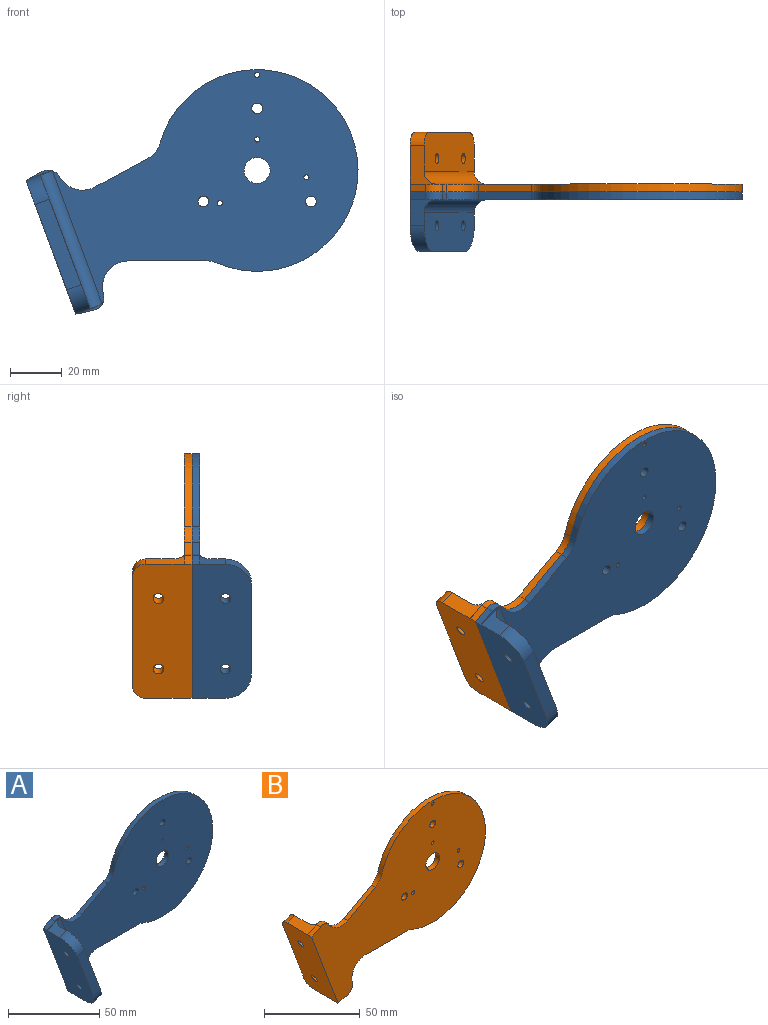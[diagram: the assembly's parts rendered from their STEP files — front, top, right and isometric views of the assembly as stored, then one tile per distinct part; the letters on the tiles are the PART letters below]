
ASSEMBLY  parts=2 mates=1
PART A: 37 faces, bbox 128.4x23x94.6 mm
  f0: plane 118.22x90.64mm, normal (0,-1,0), area 6030.9mm2, adj f6,f7,f8,f9,f10,f11,f12,f18
  f1: plane 10.12x3.79mm, normal (0,-1,0), area 6.4mm2, adj f3,f14,f27
  f2: plane 6.17x3.31mm, normal (-0.47,0,0.88), area 21mm2, adj f4,f5,f13,f26
  f3: plane 6.96x3mm, normal (0.22,0,-0.98), area 21.4mm2, adj f1,f5,f13,f27
  f4: plane 9.91x3.91mm, normal (0,-1,0), area 5.9mm2, adj f2,f15,f26
  f5: plane 128.4x94.58mm, normal (0,1,0), area 6644.3mm2, adj f2,f3,f6,f7,f8,f9,f10,f11
  f6: cylinder r=1mm len=3mm, axis (0,-1,0), area 18.8mm2, adj f0,f5
  f7: cylinder r=1mm len=3mm, axis (0,-1,0), area 18.8mm2, adj f0,f5
  f8: cylinder r=39mm len=78mm, axis (0,-1,0), area 566.8mm2, adj f0,f5,f25,f31
  f9: cylinder r=2.1mm len=4.2mm, axis (0,1,0), area 39.6mm2, adj f0,f5
  f10: cylinder r=2.1mm len=4.2mm, axis (0,1,0), area 39.6mm2, adj f0,f5
  f11: cylinder r=2.1mm len=4.2mm, axis (0,1,0), area 39.6mm2, adj f0,f5
  f12: cylinder r=5mm len=10mm, axis (0,1,0), area 94.2mm2, adj f0,f5
  f13: plane 51.83x23.01mm, normal (-0.94,0,-0.35), area 1202.4mm2, adj f2,f3,f5,f14,f15,f16,f20,f21
  f14: plane 10.12x10mm, normal (0.35,0,-0.94), area 64.8mm2, adj f1,f13,f17,f32,f35
  f15: plane 10x9.91mm, normal (-0.35,0,0.94), area 63.4mm2, adj f4,f13,f17,f34,f36
  f16: plane 35.12x17.85mm, normal (0,-1,0), area 207.3mm2, adj f13,f17,f35,f36
  f17: plane 51.77x19.41mm, normal (0.94,0,0.35), area 760mm2, adj f14,f15,f16,f20,f21,f32,f33,f34
  f18: cylinder r=1mm len=3mm, axis (0,-1,0), area 18.8mm2, adj f0,f5
  f19: cylinder r=1mm len=3mm, axis (0,-1,0), area 18.8mm2, adj f0,f5
  f20: cylinder r=2.05mm len=6.98mm, axis (0.94,0,0.35), area 76.1mm2, adj f13,f17
  f21: cylinder r=2.05mm len=6.91mm, axis (0.94,0,0.35), area 75.2mm2, adj f13,f17
  f22: plane 3x1.97mm, normal (0.79,0,0.61), area 7.5mm2, adj f0,f5,f23,f26
  f23: cylinder r=10mm len=12.64mm, axis (0,1,0), area 42.1mm2, adj f0,f5,f22,f24
  f24: plane 20.36x10.99mm, normal (-0.48,0,0.88), area 69.4mm2, adj f0,f5,f23,f25
  f25: cylinder r=10mm len=6.07mm, axis (0,1,0), area 24mm2, adj f0,f5,f8,f24
  f26: cylinder r=5mm len=6.31mm, axis (0,1,0), area 21mm2, adj f0,f2,f4,f5,f22,f34
  f27: cylinder r=5mm len=5.97mm, axis (0,1,0), area 23.6mm2, adj f0,f1,f3,f5,f28,f32
  f28: plane 3x0.92mm, normal (0.98,0,0.22), area 2.8mm2, adj f0,f5,f27,f29
  f29: cylinder r=10mm len=12.18mm, axis (0,1,0), area 53.7mm2, adj f0,f5,f28,f30
  f30: plane 30.35x3mm, normal (0,0,-1), area 91.1mm2, adj f0,f5,f29,f31
  f31: cylinder r=10mm len=3.97mm, axis (0,1,0), area 12.3mm2, adj f0,f5,f8,f30
  f32: bspline ~5.37x5.15mm, area 0.9mm2, adj f14,f17,f27,f33
  f33: cylinder r=5mm len=53.26mm, axis (-0.35,0,0.94), area 432mm2, adj f0,f17,f32,f34
  f34: bspline ~5.29x5.25mm, area 1.3mm2, adj f15,f17,f26,f33
  f35: cylinder r=10mm len=11.45mm, axis (-0.94,0,-0.35), area 93.1mm2, adj f13,f14,f16,f17
  f36: cylinder r=10mm len=11.41mm, axis (0.94,0,0.35), area 91.4mm2, adj f13,f15,f16,f17
PART B: 37 faces, bbox 128.4x23x94.6 mm
  f0: plane 10.12x3.79mm, normal (0,1,0), area 6.4mm2, adj f6,f14,f30
  f1: plane 118.22x90.64mm, normal (0,1,0), area 6030.9mm2, adj f4,f5,f7,f8,f9,f10,f11,f18
  f2: plane 6.17x3.31mm, normal (-0.47,0,0.88), area 21mm2, adj f3,f12,f13,f31
  f3: plane 128.4x94.58mm, normal (0,-1,0), area 6644.3mm2, adj f2,f4,f5,f6,f7,f8,f9,f10
  f4: cylinder r=1mm len=3mm, axis (0,1,0), area 18.8mm2, adj f1,f3
  f5: cylinder r=1mm len=3mm, axis (0,1,0), area 18.8mm2, adj f1,f3
  f6: plane 6.96x3mm, normal (0.22,0,-0.98), area 21.4mm2, adj f0,f3,f13,f30
  f7: cylinder r=39mm len=78mm, axis (0,1,0), area 566.8mm2, adj f1,f3,f27,f28
  f8: cylinder r=2.1mm len=4.2mm, axis (0,-1,0), area 39.6mm2, adj f1,f3
  f9: cylinder r=2.1mm len=4.2mm, axis (0,-1,0), area 39.6mm2, adj f1,f3
  f10: cylinder r=2.1mm len=4.2mm, axis (0,-1,0), area 39.6mm2, adj f1,f3
  f11: cylinder r=5mm len=10mm, axis (0,-1,0), area 94.2mm2, adj f1,f3
  f12: plane 9.91x3.91mm, normal (0,1,0), area 5.9mm2, adj f2,f15,f31
  f13: plane 51.83x23.01mm, normal (-0.94,0,-0.35), area 1234.6mm2, adj f2,f3,f6,f14,f15,f16,f20,f21
  f14: plane 15x10.12mm, normal (0.35,0,-0.94), area 94.5mm2, adj f0,f13,f17,f32,f36
  f15: plane 15x9.91mm, normal (-0.35,0,0.94), area 92.4mm2, adj f12,f13,f17,f34,f35
  f16: plane 44.49x21.34mm, normal (0,1,0), area 266mm2, adj f13,f17,f35,f36
  f17: plane 51.77x19.41mm, normal (0.94,0,0.35), area 792.2mm2, adj f14,f15,f16,f20,f21,f32,f33,f34
  f18: cylinder r=1mm len=3mm, axis (0,1,0), area 18.8mm2, adj f1,f3
  f19: cylinder r=1mm len=3mm, axis (0,1,0), area 18.8mm2, adj f1,f3
  f20: cylinder r=2.05mm len=6.91mm, axis (0.94,0,0.35), area 75.2mm2, adj f13,f17
  f21: cylinder r=2.05mm len=6.98mm, axis (0.94,0,0.35), area 76.1mm2, adj f13,f17
  f22: plane 30.35x3mm, normal (0,0,-1), area 91.1mm2, adj f1,f3,f26,f27
  f23: plane 3x0.92mm, normal (0.98,0,0.22), area 2.8mm2, adj f1,f3,f26,f30
  f24: plane 20.36x10.99mm, normal (-0.48,0,0.88), area 69.4mm2, adj f1,f3,f28,f29
  f25: plane 3x1.97mm, normal (0.79,0,0.61), area 7.5mm2, adj f1,f3,f29,f31
  f26: cylinder r=10mm len=12.18mm, axis (0,-1,0), area 53.7mm2, adj f1,f3,f22,f23
  f27: cylinder r=10mm len=3.97mm, axis (0,1,0), area 12.3mm2, adj f1,f3,f7,f22
  f28: cylinder r=10mm len=6.07mm, axis (0,1,0), area 24mm2, adj f1,f3,f7,f24
  f29: cylinder r=10mm len=12.64mm, axis (0,-1,0), area 42.1mm2, adj f1,f3,f24,f25
  f30: cylinder r=5mm len=5.97mm, axis (0,1,0), area 23.6mm2, adj f0,f1,f3,f6,f23,f32
  f31: cylinder r=5mm len=6.31mm, axis (0,1,0), area 21mm2, adj f1,f2,f3,f12,f25,f34
  f32: bspline ~5.37x5.15mm, area 0.9mm2, adj f14,f17,f30,f33
  f33: cylinder r=5mm len=53.26mm, axis (-0.35,0,0.94), area 432mm2, adj f1,f17,f32,f34
  f34: bspline ~5.29x5.25mm, area 1.3mm2, adj f15,f17,f31,f33
  f35: cylinder r=5mm len=7.2mm, axis (0.94,0,0.35), area 45.6mm2, adj f13,f15,f16,f17
  f36: cylinder r=5mm len=7.32mm, axis (-0.94,0,-0.35), area 46.6mm2, adj f13,f14,f16,f17
PLACE A t=(23.09,66.18,-3.22)mm
PLACE B t=(23.09,50.18,-3.22)mm
MATE fastened A.f8 <-> B.f7  axis (0,1,0) through (23.09,47.18,-3.22)mm
